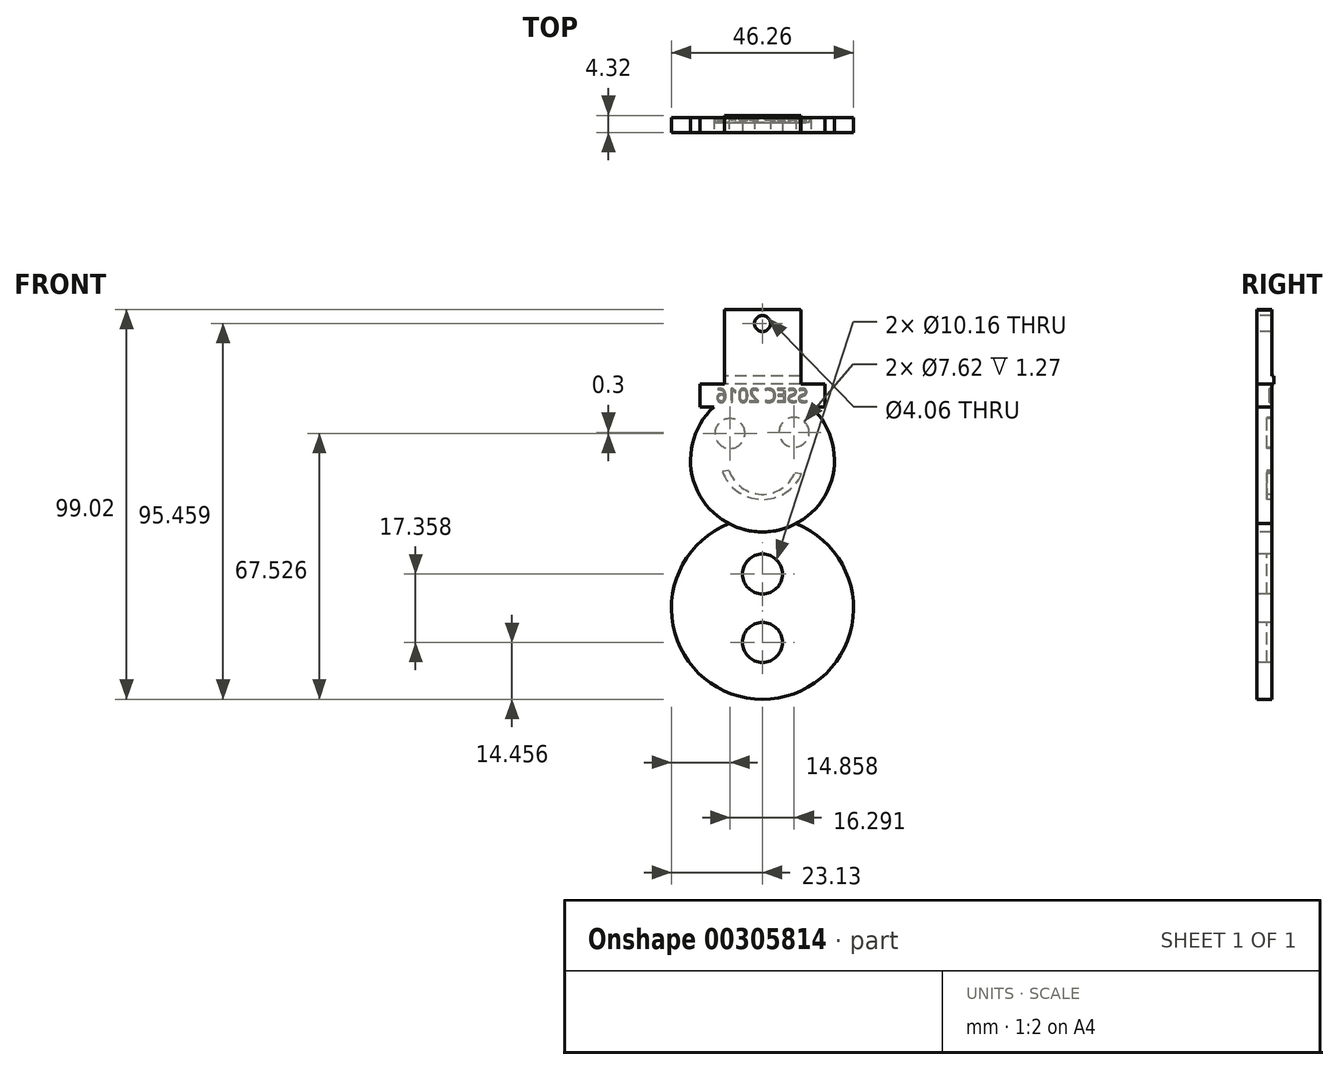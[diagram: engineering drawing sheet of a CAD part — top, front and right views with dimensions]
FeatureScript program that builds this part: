
annotation { "Feature Type Name" : "Feature", "Feature Type Description" : "" }
export const myFeature = defineFeature(function(context is Context, id is Id, definition is map)
    precondition{}
    {
        {
            var Q0;
            Q0=qCreatedBy(makeId("Front.planeOp"),FACE);
            var sketch = newSketch(context, id + "F0", { "sketchPlane" : qUnion([Q0])});
            skCircle(sketch, "E0", {"center": v(0, -37.67) * mm, "radius": 23.13 * mm});
            skArc(sketch, "E1", {"start": v(-12.32, 13.5) * mm, "mid": v(0, -18.28) * mm, "end": v(12.32, 13.5) * mm});
            skLineSegment(sketch, "E2.top", {"start": v(-15.85, 13.5) * mm, "end": v(15.85, 13.5) * mm});
            skLineSegment(sketch, "E2.left", {"start": v(-15.85, 19.24) * mm, "end": v(-15.85, 13.5) * mm});
            skLineSegment(sketch, "E2.right", {"start": v(15.85, 19.24) * mm, "end": v(15.85, 13.5) * mm});
            skLineSegment(sketch, "E3.top", {"start": v(-9.65, 38.22) * mm, "end": v(9.65, 38.22) * mm});
            skLineSegment(sketch, "E3.left", {"start": v(-9.65, 19.24) * mm, "end": v(-9.65, 38.22) * mm});
            skLineSegment(sketch, "E3.right", {"start": v(9.65, 19.24) * mm, "end": v(9.65, 38.22) * mm});
            skCircle(sketch, "E4", {"center": v(-8.27, 6.73) * mm, "radius": 3.81 * mm});
            skCircle(sketch, "E5", {"center": v(8.02, 7.03) * mm, "radius": 3.81 * mm});
            skArc(sketch, "E6", {"start": v(-10.2, -2.86) * mm, "mid": v(-0.31, -10.02) * mm, "end": v(9.97, -3.45) * mm});
            skArc(sketch, "E7", {"start": v(-8.49, -2.64) * mm, "mid": v(-0.3, -8.72) * mm, "end": v(8.28, -3.2) * mm});
            skLineSegment(sketch, "E8", {"start": v(-8.49, -2.64) * mm, "end": v(-10.2, -2.86) * mm});
            skLineSegment(sketch, "E9", {"start": v(8.28, -3.2) * mm, "end": v(9.97, -3.45) * mm});
            skCircle(sketch, "E10", {"center": v(0, -28.99) * mm, "radius": 5.08 * mm});
            skCircle(sketch, "E11", {"center": v(0, -46.34) * mm, "radius": 5.08 * mm});
            skCircle(sketch, "E12", {"center": v(0, 34.66) * mm, "radius": 2.03 * mm});
            skLineSegment(sketch, "E13.trimOffspring", {"start": v(9.65, 19.24) * mm, "end": v(15.85, 19.24) * mm});
            skLineSegment(sketch, "E14", {"start": v(-9.65, 19.24) * mm, "end": v(-15.85, 19.24) * mm});
            skSolve(sketch);
        }
        {
            var Q0;
            Q0=makeQuery(id+"F0.imprint","IMPRINT",FACE,{"disambiguationData":[TD([[makeQuery(id+"F0.imprint","IMPRINT",EDGE,{"derivedFrom":sQuery(id+"F0.wireOp",EDGE,"E3.bottom")}),1.0]])]});
            var Q1;
            {var subQ14=sQuery(id+"F0.wireOp",EDGE,"E2.left");Q1=makeQuery(id+"F0.imprint","IMPRINT",FACE,{"disambiguationData":[TD([[makeQuery(id+"F0.imprint","IMPRINT",EDGE,{"derivedFrom":subQ14}),1.0]])]});}
            var Q2;
            Q2=makeQuery(id+"F0.imprint","IMPRINT",FACE,{"disambiguationData":[TD([[makeQuery(id+"F0.imprint","IMPRINT",EDGE,{"derivedFrom":sQuery(id+"F0.wireOp",EDGE,"E4")}),-1.0]])]});
            var Q3;
            {var subQ0=sQuery(id+"F0.wireOp",EDGE,"E1");var subQ1=sQuery(id+"F0.wireOp",EDGE,"E0");var subQ2=makeQuery(id+"F0.imprint","INTERSECT",VERTEX,{"disambiguationData":[OD(0.0)],"derivedFrom":[subQ1,subQ0]});Q3=makeQuery(id+"F0.imprint","IMPRINT",FACE,{"disambiguationData":[TD([[makeQuery(id+"F0.imprint","IMPRINT",EDGE,{"disambiguationData":[TD([[subQ2,-1.0]])],"derivedFrom":subQ1}),1.0]])]});}
            var Q4;
            Q4=makeQuery(id+"F0.imprint","IMPRINT",FACE,{"disambiguationData":[TD([[makeQuery(id+"F0.imprint","IMPRINT",EDGE,{"derivedFrom":sQuery(id+"F0.wireOp",EDGE,"d47015dd-9014-4c70-bc6b-3e0848645b5b.sketch_text.stroke-0")}),1.0]])]});
            var Q5;
            Q5=makeQuery(id+"F0.imprint","IMPRINT",FACE,{"disambiguationData":[TD([[makeQuery(id+"F0.imprint","IMPRINT",EDGE,{"derivedFrom":sQuery(id+"F0.wireOp",EDGE,"d47015dd-9014-4c70-bc6b-3e0848645b5b.sketch_text.stroke-105")}),1.0]])]});
            var Q6;
            {var subQ0=sQuery(id+"F0.wireOp",EDGE,"d47015dd-9014-4c70-bc6b-3e0848645b5b.sketch_text.stroke-139");Q6=makeQuery(id+"F0.imprint","IMPRINT",FACE,{"disambiguationData":[TD([[makeQuery(id+"F0.imprint","IMPRINT",EDGE,{"derivedFrom":subQ0}),1.0]])]});}
            var Q7;
            {var subQ0=sQuery(id+"F0.wireOp",EDGE,"d47015dd-9014-4c70-bc6b-3e0848645b5b.sketch_text.stroke-5");Q7=makeQuery(id+"F0.imprint","IMPRINT",FACE,{"disambiguationData":[TD([[makeQuery(id+"F0.imprint","IMPRINT",EDGE,{"derivedFrom":subQ0}),1.0]])]});}
            var Q8;
            {var subQ5=sQuery(id+"F0.wireOp",EDGE,"d47015dd-9014-4c70-bc6b-3e0848645b5b.sketch_text.stroke-137");Q8=makeQuery(id+"F0.imprint","IMPRINT",FACE,{"disambiguationData":[TD([[makeQuery(id+"F0.imprint","IMPRINT",EDGE,{"derivedFrom":subQ5}),1.0]])]});}
            extrude(context, id + "F1", {"entities" : qUnion([Q0, Q1, Q2, Q3, Q4, Q5, Q6, Q7, Q8]), "oppositeDirection" : true, "depth" : 3.8 * mm});
        }
        {
            var Q0;
            {var subQ0=sQuery(id+"F0.wireOp",EDGE,"E1");var subQ1=sQuery(id+"F0.wireOp",EDGE,"E0");var subQ2=makeQuery(id+"F0.imprint","INTERSECT",VERTEX,{"disambiguationData":[OD(0.0)],"derivedFrom":[subQ1,subQ0]});Q0=makeQuery(id+"F0.imprint","IMPRINT",FACE,{"disambiguationData":[TD([[makeQuery(id+"F0.imprint","IMPRINT",EDGE,{"disambiguationData":[TD([[subQ2,1.0]])],"derivedFrom":subQ1}),1.0]])]});}
            extrude(context, id + "F2", {"entities" : qUnion([Q0]), "oppositeDirection" : true, "depth" : 3.8 * mm});
        }
        {
            var Q0;
            Q0=makeQuery(id+"F0.imprint","IMPRINT",FACE,{"disambiguationData":[TD([[makeQuery(id+"F0.imprint","IMPRINT",EDGE,{"derivedFrom":sQuery(id+"F0.wireOp",EDGE,"E4")}),1.0]])]});
            var Q1;
            Q1=makeQuery(id+"F0.imprint","IMPRINT",FACE,{"disambiguationData":[TD([[makeQuery(id+"F0.imprint","IMPRINT",EDGE,{"derivedFrom":sQuery(id+"F0.wireOp",EDGE,"E5")}),1.0]])]});
            extrude(context, id + "F3", {"entities" : qUnion([Q0, Q1]), "operationType" : NewBodyOperationType.ADD, "oppositeDirection" : true, "depth" : 2.54 * mm});
        }
        {
            var Q0;
            Q0=qCreatedBy(makeId("Front.planeOp"),FACE);
            var sketch = newSketch(context, id + "F4", { "sketchPlane" : qUnion([Q0])});
            skCircle(sketch, "E15", {"center": v(0, -37.76) * mm, "radius": 23.13 * mm});
            skCircle(sketch, "E16", {"center": v(0, -0.08) * mm, "radius": 18.28 * mm});
            skLineSegment(sketch, "E17.bottom", {"start": v(-15.85, 19.16) * mm, "end": v(15.85, 19.16) * mm});
            skLineSegment(sketch, "E17.left", {"start": v(-15.85, 19.16) * mm, "end": v(-15.85, 13.42) * mm});
            skLineSegment(sketch, "E17.right", {"start": v(15.85, 19.16) * mm, "end": v(15.85, 13.42) * mm});
            skLineSegment(sketch, "E18.top", {"start": v(-9.12, 38.14) * mm, "end": v(9.77, 38.14) * mm});
            skLineSegment(sketch, "E18.left", {"start": v(-9.12, 19.16) * mm, "end": v(-9.12, 38.14) * mm});
            skLineSegment(sketch, "E18.right", {"start": v(9.77, 19.16) * mm, "end": v(9.77, 38.14) * mm});
            skSolve(sketch);
        }
        {
            var Q0;
            Q0=makeQuery(id+"F0.imprint","IMPRINT",FACE,{"disambiguationData":[TD([[makeQuery(id+"F0.imprint","IMPRINT",EDGE,{"derivedFrom":sQuery(id+"F0.wireOp",EDGE,"E6")}),1.0]])]});
            extrude(context, id + "F5", {"entities" : qUnion([Q0]), "operationType" : NewBodyOperationType.ADD, "oppositeDirection" : true, "depth" : 2.54 * mm});
        }
        {
            var Q0;
            Q0=makeQuery(id+"F0.imprint","IMPRINT",FACE,{"disambiguationData":[TD([[makeQuery(id+"F0.imprint","IMPRINT",EDGE,{"derivedFrom":sQuery(id+"F0.wireOp",EDGE,"E11")}),1.0]])]});
            var Q1;
            Q1=makeQuery(id+"F0.imprint","IMPRINT",FACE,{"disambiguationData":[TD([[makeQuery(id+"F0.imprint","IMPRINT",EDGE,{"derivedFrom":sQuery(id+"F0.wireOp",EDGE,"E10")}),1.0]])]});
            extrude(context, id + "F6", {"entities" : qUnion([Q0, Q1]), "oppositeDirection" : true, "depth" : 2.54 * mm});
        }
        {
            var Q0;
            Q0=makeQuery(id+"F4.imprint","IMPRINT",FACE,{"disambiguationData":[TD([[makeQuery(id+"F4.imprint","IMPRINT",EDGE,{"derivedFrom":sQuery(id+"F4.wireOp",EDGE,"E18.top")}),-1.0]])]});
            extrude(context, id + "F7", {"entities" : qUnion([Q0]), "operationType" : NewBodyOperationType.ADD, "oppositeDirection" : true, "depth" : 3.8 * mm});
        }
        {
            var Q0;
            Q0=makeQuery(id+"F7.boolean.opBoolean","MERGE",FACE,{"derivedFrom":[makeQuery(id+"F1.opExtrude","CAP_FACE",FACE,{"disambiguationData":[OSD([sQuery(id+"F0.wireOp",EDGE,"E1"),sQuery(id+"F0.wireOp",EDGE,"E2.top"),sQuery(id+"F0.wireOp",EDGE,"E2.left"),sQuery(id+"F0.wireOp",EDGE,"E2.right"),sQuery(id+"F0.wireOp",EDGE,"E3.top"),sQuery(id+"F0.wireOp",EDGE,"E3.left"),sQuery(id+"F0.wireOp",EDGE,"E3.right"),sQuery(id+"F0.wireOp",EDGE,"E12"),sQuery(id+"F0.wireOp",EDGE,"E13.trimOffspring"),sQuery(id+"F0.wireOp",EDGE,"E14")])],"isStart":false}),makeQuery(id+"F7.opExtrude","CAP_FACE",FACE,{"disambiguationData":[OSD([sQuery(id+"F4.wireOp",EDGE,"E17.bottom"),sQuery(id+"F4.wireOp",EDGE,"E18.top"),sQuery(id+"F4.wireOp",EDGE,"E18.left"),sQuery(id+"F4.wireOp",EDGE,"E18.right")])],"isStart":false})]});
            var sketch = newSketch(context, id + "F8", { "sketchPlane" : qUnion([Q0])});
            skLineSegment(sketch, "E19.bottom", {"start": v(-9.77, 19.24) * mm, "end": v(9.65, 19.24) * mm});
            skLineSegment(sketch, "E19.top", {"start": v(-9.77, 21.38) * mm, "end": v(9.65, 21.38) * mm});
            skLineSegment(sketch, "E19.left", {"start": v(-9.77, 19.24) * mm, "end": v(-9.77, 21.38) * mm});
            skLineSegment(sketch, "E19.right", {"start": v(9.65, 19.24) * mm, "end": v(9.65, 21.38) * mm});
            skSolve(sketch);
        }
        {
            var Q0;
            Q0=makeQuery(id+"F8.imprint","IMPRINT",FACE,{"disambiguationData":[TD([[makeQuery(id+"F8.imprint","IMPRINT",EDGE,{"derivedFrom":sQuery(id+"F8.wireOp",EDGE,"E19.bottom")}),1.0]])]});
            extrude(context, id + "F9", {"entities" : qUnion([Q0]), "operationType" : NewBodyOperationType.ADD, "depth" : 0.5 * mm});
        }
        {
            var Q0;
            {var subQ0=sQuery(id+"F0.wireOp",EDGE,"E4");var subQ1=sQuery(id+"F0.wireOp",EDGE,"E3.left");var subQ2=sQuery(id+"F0.wireOp",EDGE,"E2.right");var subQ3=sQuery(id+"F0.wireOp",EDGE,"E2.top");var subQ4=sQuery(id+"F0.wireOp",EDGE,"E1");var subQ6=sQuery(id+"F0.wireOp",EDGE,"E2.left");var subQ7=sQuery(id+"F0.wireOp",EDGE,"E0");var subQ10=sQuery(id+"F0.wireOp",EDGE,"E5");var subQ12=sQuery(id+"F0.wireOp",EDGE,"E6");var subQ13=sQuery(id+"F0.wireOp",EDGE,"E7");var subQ14=sQuery(id+"F0.wireOp",EDGE,"E8");var subQ15=sQuery(id+"F0.wireOp",EDGE,"E9");var subQ16=sQuery(id+"F4.wireOp",EDGE,"E18.right");var subQ17=sQuery(id+"F0.wireOp",EDGE,"E13.trimOffspring");var subQ18=sQuery(id+"F0.wireOp",EDGE,"E14");Q0=makeQuery(id+"F9.boolean.opBoolean","SPLIT",FACE,{"disambiguationData":[TD([makeQuery(id+"F1.opExtrude","SWEPT_FACE",FACE,{"disambiguationData":[OSD([subQ6])]})])],"derivedFrom":makeQuery(id+"F7.boolean.opBoolean","MERGE",FACE,{"derivedFrom":[makeQuery(id+"F1.opExtrude","CAP_FACE",FACE,{"disambiguationData":[OSD([subQ7,subQ4,subQ3,subQ6,subQ2,sQuery(id+"F0.wireOp",EDGE,"E3.top"),subQ1,sQuery(id+"F0.wireOp",EDGE,"E3.right"),subQ0,subQ10,subQ12,subQ13,subQ14,subQ15,sQuery(id+"F0.wireOp",EDGE,"E12"),subQ17,subQ18])],"isStart":false}),makeQuery(id+"F7.opExtrude","CAP_FACE",FACE,{"disambiguationData":[OSD([sQuery(id+"F4.wireOp",EDGE,"E17.bottom"),sQuery(id+"F4.wireOp",EDGE,"E18.top"),sQuery(id+"F4.wireOp",EDGE,"E18.left"),subQ16])],"isStart":false})]})});}
            var sketch = newSketch(context, id + "F10", { "sketchPlane" : qUnion([Q0])});
            skText(sketch, "E20", { "text": "SSEC 2016\n", "fontName": "OpenSans-Regular.ttf"});
            const initialGuessF10  = {"E20": [-0.01156, 0.01467, 1, 0, 0.00348]};
            skSetInitialGuess(sketch, initialGuessF10);
            skSolve(sketch);
        }
        {
            var Q0;
            Q0 = qSketchRegion(id + "F10", true);
            extrude(context, id + "F11", {"entities" : qUnion([Q0]), "operationType" : NewBodyOperationType.REMOVE, "oppositeDirection" : true, "depth" : 0.64 * mm});
        }
        {
            var Q0;
            Q0=makeQuery(id+"F0.imprint","IMPRINT",FACE,{"disambiguationData":[TD([[makeQuery(id+"F0.imprint","IMPRINT",EDGE,{"derivedFrom":sQuery(id+"F0.wireOp",EDGE,"E12")}),1.0]])]});
            extrude(context, id + "F12", {"entities" : qUnion([Q0]), "operationType" : NewBodyOperationType.REMOVE, "oppositeDirection" : true, "depth" : 25.4 * mm});
        }
    });
